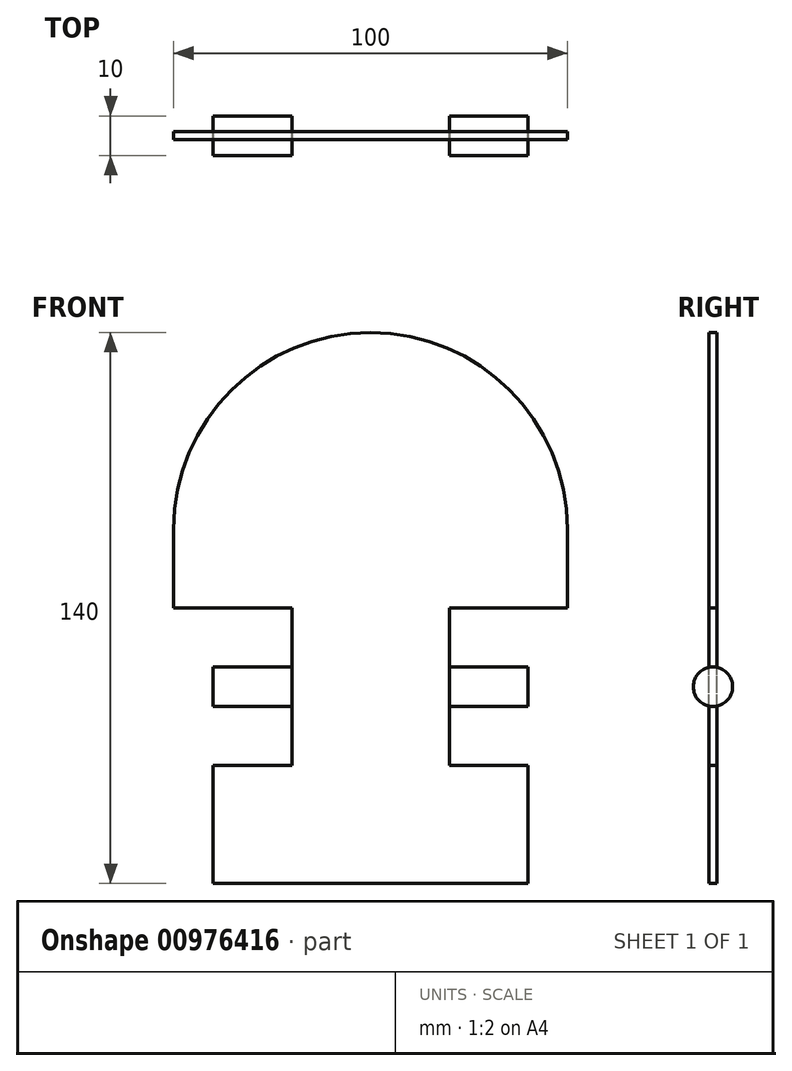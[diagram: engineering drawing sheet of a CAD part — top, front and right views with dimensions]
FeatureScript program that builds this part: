
annotation { "Feature Type Name" : "Feature", "Feature Type Description" : "" }
export const myFeature = defineFeature(function(context is Context, id is Id, definition is map)
    precondition{}
    {
        {
            var Q0;
            Q0=qCreatedBy(makeId("Front.planeOp"),FACE);
            var sketch = newSketch(context, id + "F0", { "sketchPlane" : qUnion([Q0])});
            skLineSegment(sketch, "E0", {"start": v(0, -50) * mm, "end": v(-40, -50) * mm});
            skLineSegment(sketch, "E1", {"start": v(-40, -50) * mm, "end": v(-40, -20) * mm});
            skLineSegment(sketch, "E2", {"start": v(-40, -20) * mm, "end": v(-20, -20) * mm});
            skLineSegment(sketch, "E3", {"start": v(-20, -20) * mm, "end": v(-20, 20) * mm});
            skLineSegment(sketch, "E4", {"start": v(-20, 20) * mm, "end": v(-50, 20) * mm});
            skLineSegment(sketch, "E5", {"start": v(-50, 20) * mm, "end": v(-50, 40) * mm});
            skLineSegment(sketch, "E6", {"start": v(-50, 40) * mm, "end": v(0, 40) * mm, "construction": true});
            skArc(sketch, "E7", {"start": v(-50, 40) * mm, "mid": v(-35.36, 75.36) * mm, "end": v(0, 90) * mm});
            skLineSegment(sketch, "E8", {"start": v(-20, 0) * mm, "end": v(0, 0) * mm, "construction": true});
            skLineSegment(sketch, "E9", {"start": v(0, 90) * mm, "end": v(0, -50) * mm, "construction": true});
            skLineSegment(sketch, "E10.MirrorCS", {"start": v(20, 20) * mm, "end": v(50, 20) * mm});
            skLineSegment(sketch, "E11.MirrorCS", {"start": v(50, 40) * mm, "end": v(0, 40) * mm, "construction": true});
            skLineSegment(sketch, "E12.MirrorCS", {"start": v(20, 0) * mm, "end": v(0, 0) * mm, "construction": true});
            skLineSegment(sketch, "E13.MirrorCS", {"start": v(40, -50) * mm, "end": v(40, -20) * mm});
            skLineSegment(sketch, "E14.MirrorCS", {"start": v(40, -20) * mm, "end": v(20, -20) * mm});
            skArc(sketch, "E15.MirrorCS", {"start": v(50, 40) * mm, "mid": v(35.36, 75.36) * mm, "end": v(0, 90) * mm});
            skLineSegment(sketch, "E16.MirrorCS", {"start": v(0, -50) * mm, "end": v(40, -50) * mm});
            skLineSegment(sketch, "E17.MirrorCS", {"start": v(20, -20) * mm, "end": v(20, 20) * mm});
            skLineSegment(sketch, "E18.MirrorCS", {"start": v(50, 20) * mm, "end": v(50, 40) * mm});
            skSolve(sketch);
        }
        {
            var Q0;
            Q0 = qSketchRegion(id + "F0", true);
            extrude(context, id + "F1", {"entities" : qUnion([Q0]), "oppositeDirection" : true, "depth" : 2 * mm, "offsetDistance" : 25 * mm});
        }
        {
            var Q0;
            Q0=makeQuery(id+"F1.opExtrude","SWEPT_FACE",FACE,{"disambiguationData":[OSD([sQuery(id+"F0.wireOp",EDGE,"E3")])]});
            var sketch = newSketch(context, id + "F2", { "sketchPlane" : qUnion([Q0])});
            skLineSegment(sketch, "E19", {"start": v(-2, 0) * mm, "end": v(0, 0) * mm, "construction": true});
            skCircle(sketch, "E20", {"center": v(-1, 0) * mm, "radius": 5 * mm});
            skSolve(sketch);
        }
        {
            var Q0;
            Q0 = qSketchRegion(id + "F2", true);
            extrude(context, id + "F3", {"entities" : qUnion([Q0]), "depth" : 20 * mm, "offsetDistance" : 25 * mm});
        }
        {
            var Q0;
            Q0=makeQuery(id+"F3.opExtrude","SWEPT_BODY",BODY,{"disambiguationData":[OSD([sQuery(id+"F2.wireOp",EDGE,"E20")])]});
            var Q1;
            Q1=qCreatedBy(makeId("Right.planeOp"),FACE);
            mirror(context, id + "F4", {"entities" : qUnion([Q0]), "mirrorPlane" : qUnion([Q1])});
        }
    });
